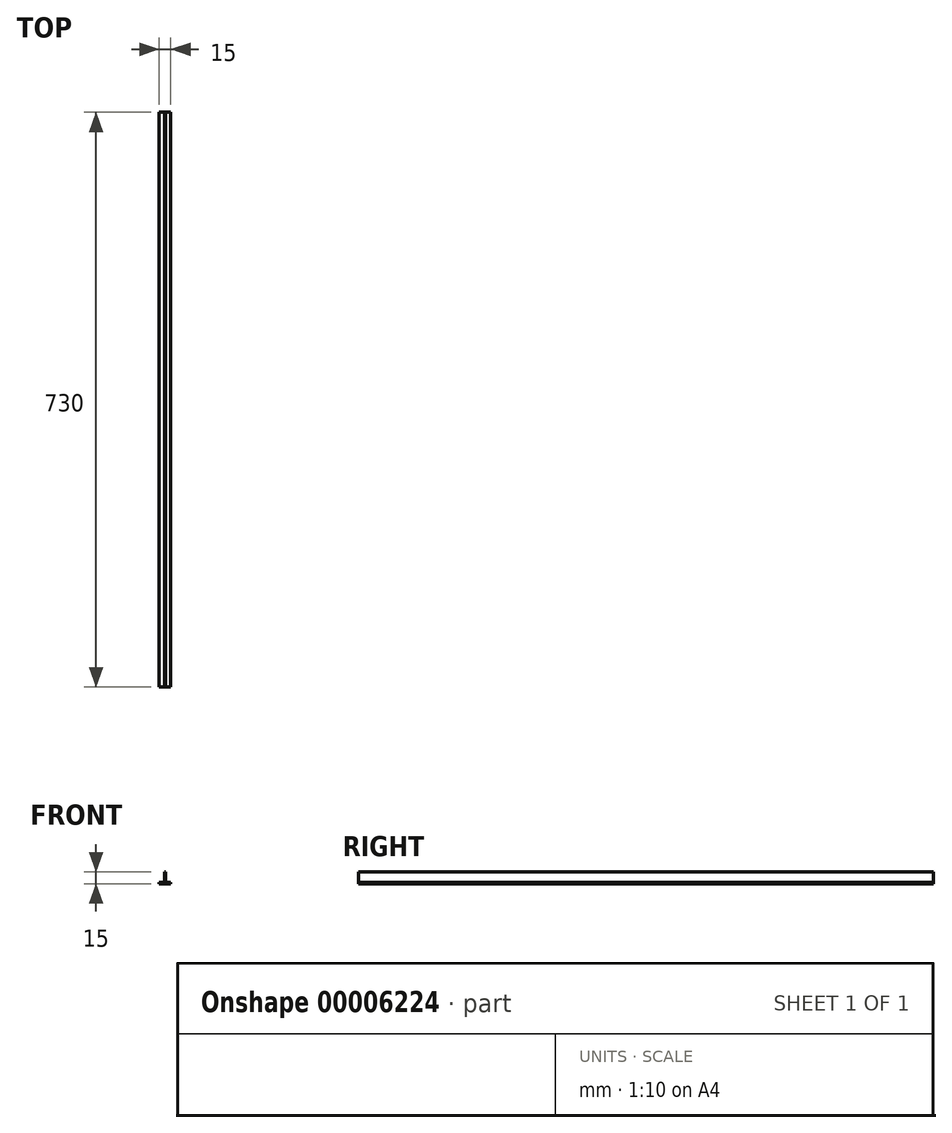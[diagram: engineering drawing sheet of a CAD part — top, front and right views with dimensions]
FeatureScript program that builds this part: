
annotation { "Feature Type Name" : "Feature", "Feature Type Description" : "" }
export const myFeature = defineFeature(function(context is Context, id is Id, definition is map)
    precondition{}
    {
        {
            var Q0;
            Q0=qCreatedBy(makeId("Front.planeOp"),FACE);
            var sketch = newSketch(context, id + "F0", { "sketchPlane" : qUnion([Q0])});
            skLineSegment(sketch, "E0.rect.bottom", {"start": v(7.5, 0.75) * mm, "end": v(0.75, 0.75) * mm});
            skLineSegment(sketch, "E0.rect.top", {"start": v(7.5, -0.75) * mm, "end": v(-7.5, -0.75) * mm});
            skLineSegment(sketch, "E0.rect.left", {"start": v(7.5, 0.75) * mm, "end": v(7.5, -0.75) * mm});
            skLineSegment(sketch, "E0.rect.right", {"start": v(-7.5, 0.75) * mm, "end": v(-7.5, -0.75) * mm});
            skPoint(sketch, "E0.rect.middle", {"position": v(0, 0) * mm});
            skLineSegment(sketch, "E1.rect.bottom", {"start": v(0.75, 14.25) * mm, "end": v(-0.75, 14.25) * mm});
            skLineSegment(sketch, "E1.rect.left", {"start": v(0.75, 14.25) * mm, "end": v(0.75, 0.75) * mm});
            skLineSegment(sketch, "E1.rect.right", {"start": v(-0.75, 14.25) * mm, "end": v(-0.75, 0.75) * mm});
            skPoint(sketch, "E1.rect.top.start.orphan", {"position": v(0.75, -14.25) * mm});
            skPoint(sketch, "E2.orphan", {"position": v(-0.75, -14.25) * mm});
            skLineSegment(sketch, "E3.trimOffspring", {"start": v(-0.75, 0.75) * mm, "end": v(-7.5, 0.75) * mm});
            skSolve(sketch);
        }
        {
            var Q0;
            Q0 = qSketchRegion(id + "F0", true);
            extrude(context, id + "F1", {"entities" : qUnion([Q0]), "depth" : 730 * mm});
        }
    });
